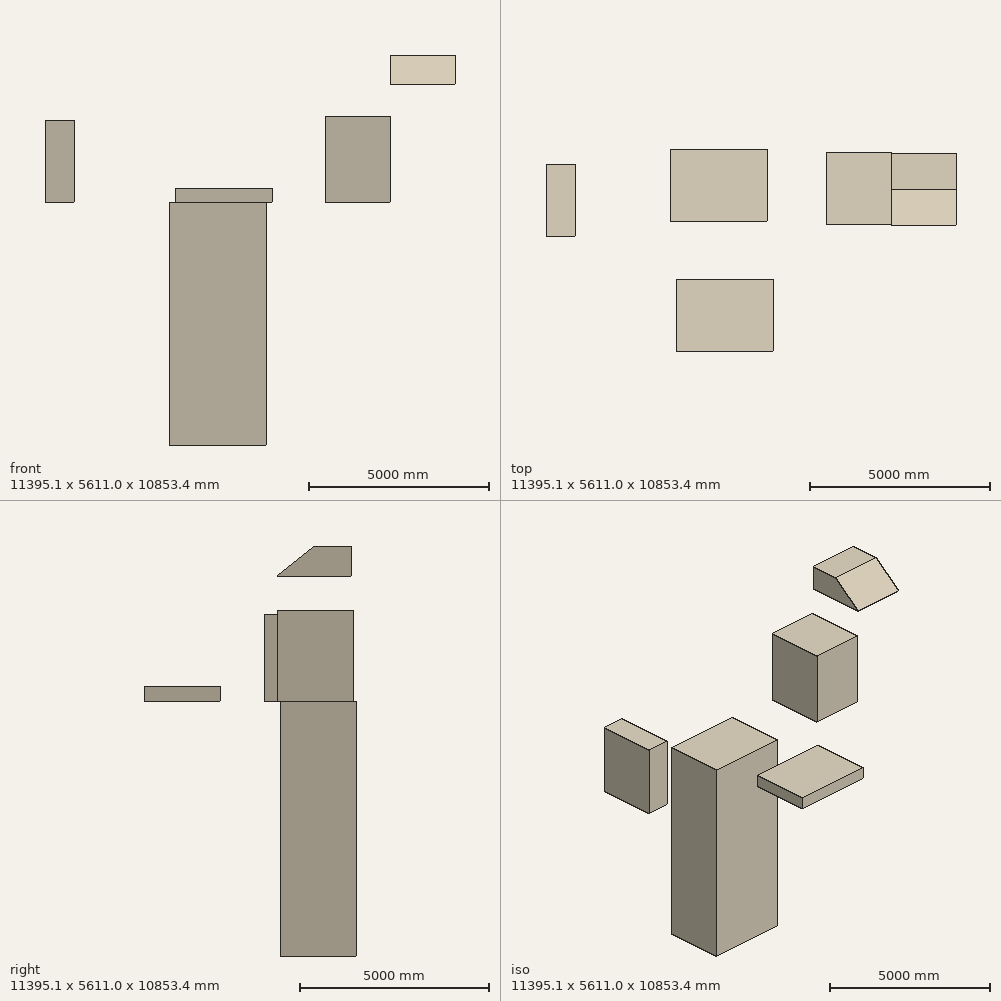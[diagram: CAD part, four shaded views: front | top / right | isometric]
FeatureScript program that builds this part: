
annotation { "Feature Type Name" : "Feature", "Feature Type Description" : "" }
export const myFeature = defineFeature(function(context is Context, id is Id, definition is map)
    precondition{}
    {
        {
            var Q0;
            Q0=qCreatedBy(makeId("Top.planeOp"),FACE);
            var sketch = newSketch(context, id + "F0", { "sketchPlane" : qUnion([Q0])});
            skLineSegment(sketch, "E0.bottom", {"start": v(-262.1, 1993.38) * mm, "end": v(2437.9, 1993.38) * mm});
            skLineSegment(sketch, "E0.top", {"start": v(-262.1, -6.62) * mm, "end": v(2437.9, -6.62) * mm});
            skLineSegment(sketch, "E0.left", {"start": v(-262.1, 1993.38) * mm, "end": v(-262.1, -6.62) * mm});
            skLineSegment(sketch, "E0.right", {"start": v(2437.9, 1993.38) * mm, "end": v(2437.9, -6.62) * mm});
            skSolve(sketch);
        }
        {
            var Q0;
            Q0=makeQuery(id+"F0.imprint","IMPRINT",FACE,{"disambiguationData":[TD([[makeQuery(id+"F0.imprint","IMPRINT",EDGE,{"derivedFrom":sQuery(id+"F0.wireOp",EDGE,"E0.bottom")}),-1.0]])]});
            extrude(context, id + "F1", {"entities" : qUnion([Q0]), "depth" : 6750 * mm, "offsetDistance" : 25 * mm});
        }
        {
            var Q0;
            Q0=makeQuery(id+"F1.opExtrude","CAP_FACE",FACE,{"disambiguationData":[OSD([sQuery(id+"F0.wireOp",EDGE,"E0.bottom"),sQuery(id+"F0.wireOp",EDGE,"E0.top"),sQuery(id+"F0.wireOp",EDGE,"E0.left"),sQuery(id+"F0.wireOp",EDGE,"E0.right")])],"isStart":false});
            var sketch = newSketch(context, id + "F2", { "sketchPlane" : qUnion([Q0])});
            skLineSegment(sketch, "E1.bottom", {"start": v(-80.11, -1617.65) * mm, "end": v(2619.89, -1617.65) * mm});
            skLineSegment(sketch, "E1.top", {"start": v(-80.11, -3617.65) * mm, "end": v(2619.89, -3617.65) * mm});
            skLineSegment(sketch, "E1.left", {"start": v(-80.11, -1617.65) * mm, "end": v(-80.11, -3617.65) * mm});
            skLineSegment(sketch, "E1.right", {"start": v(2619.89, -1617.65) * mm, "end": v(2619.89, -3617.65) * mm});
            skSolve(sketch);
        }
        {
            var Q0;
            Q0=makeQuery(id+"F2.imprint","IMPRINT",FACE,{"disambiguationData":[TD([[makeQuery(id+"F2.imprint","IMPRINT",EDGE,{"derivedFrom":sQuery(id+"F2.wireOp",EDGE,"E1.bottom")}),-1.0]])]});
            extrude(context, id + "F3", {"entities" : qUnion([Q0]), "depth" : 400 * mm, "offsetDistance" : 25 * mm});
        }
        {
            var Q0;
            Q0=makeQuery(id+"F1.opExtrude","CAP_FACE",FACE,{"disambiguationData":[OSD([sQuery(id+"F0.wireOp",EDGE,"E0.bottom"),sQuery(id+"F0.wireOp",EDGE,"E0.top"),sQuery(id+"F0.wireOp",EDGE,"E0.left"),sQuery(id+"F0.wireOp",EDGE,"E0.right")])],"isStart":false});
            var sketch = newSketch(context, id + "F4", { "sketchPlane" : qUnion([Q0])});
            skLineSegment(sketch, "E2.bottom", {"start": v(-3695.63, 1571.36) * mm, "end": v(-2895.63, 1571.36) * mm});
            skLineSegment(sketch, "E2.top", {"start": v(-3695.63, -428.64) * mm, "end": v(-2895.63, -428.64) * mm});
            skLineSegment(sketch, "E2.left", {"start": v(-3695.63, 1571.36) * mm, "end": v(-3695.63, -428.64) * mm});
            skLineSegment(sketch, "E2.right", {"start": v(-2895.63, 1571.36) * mm, "end": v(-2895.63, -428.64) * mm});
            skSolve(sketch);
        }
        {
            var Q0;
            Q0=makeQuery(id+"F4.imprint","IMPRINT",FACE,{"disambiguationData":[TD([[makeQuery(id+"F4.imprint","IMPRINT",EDGE,{"derivedFrom":sQuery(id+"F4.wireOp",EDGE,"E2.bottom")}),-1.0]])]});
            extrude(context, id + "F5", {"entities" : qUnion([Q0]), "depth" : 2300 * mm, "offsetDistance" : 25 * mm});
        }
        {
            var Q0;
            Q0=makeQuery(id+"F1.opExtrude","CAP_FACE",FACE,{"disambiguationData":[OSD([sQuery(id+"F0.wireOp",EDGE,"E0.bottom"),sQuery(id+"F0.wireOp",EDGE,"E0.top"),sQuery(id+"F0.wireOp",EDGE,"E0.left"),sQuery(id+"F0.wireOp",EDGE,"E0.right")])],"isStart":false});
            var sketch = newSketch(context, id + "F6", { "sketchPlane" : qUnion([Q0])});
            skLineSegment(sketch, "E3.bottom", {"start": v(4099.52, 1901.11) * mm, "end": v(5899.52, 1901.11) * mm});
            skLineSegment(sketch, "E3.top", {"start": v(4099.52, -98.89) * mm, "end": v(5899.52, -98.89) * mm});
            skLineSegment(sketch, "E3.left", {"start": v(4099.52, 1901.11) * mm, "end": v(4099.52, -98.89) * mm});
            skLineSegment(sketch, "E3.right", {"start": v(5899.52, 1901.11) * mm, "end": v(5899.52, -98.89) * mm});
            skSolve(sketch);
        }
        {
            var Q0;
            Q0=makeQuery(id+"F6.imprint","IMPRINT",FACE,{"disambiguationData":[TD([[makeQuery(id+"F6.imprint","IMPRINT",EDGE,{"derivedFrom":sQuery(id+"F6.wireOp",EDGE,"E3.bottom")}),-1.0]])]});
            extrude(context, id + "F7", {"entities" : qUnion([Q0]), "depth" : 2400 * mm, "offsetDistance" : 25 * mm});
        }
        {
            var Q0;
            Q0=makeQuery(id+"F7.opExtrude","SWEPT_FACE",FACE,{"disambiguationData":[OSD([sQuery(id+"F6.wireOp",EDGE,"E3.right")])]});
            var sketch = newSketch(context, id + "F8", { "sketchPlane" : qUnion([Q0])});
            skLineSegment(sketch, "E4", {"start": v(-126.47, 10053.44) * mm, "end": v(1873.53, 10053.44) * mm});
            skLineSegment(sketch, "E5", {"start": v(1873.53, 10053.44) * mm, "end": v(1873.53, 10853.44) * mm});
            skLineSegment(sketch, "E6", {"start": v(1873.53, 10853.44) * mm, "end": v(873.53, 10853.44) * mm});
            skLineSegment(sketch, "E7", {"start": v(873.53, 10853.44) * mm, "end": v(-126.47, 10053.44) * mm});
            skSolve(sketch);
        }
        {
            var Q0;
            Q0=makeQuery(id+"F8.imprint","IMPRINT",FACE,{"disambiguationData":[TD([[makeQuery(id+"F8.imprint","IMPRINT",EDGE,{"derivedFrom":sQuery(id+"F8.wireOp",EDGE,"E4")}),1.0]])]});
            extrude(context, id + "F9", {"entities" : qUnion([Q0]), "depth" : 1800 * mm, "offsetDistance" : 25 * mm});
        }
    });
